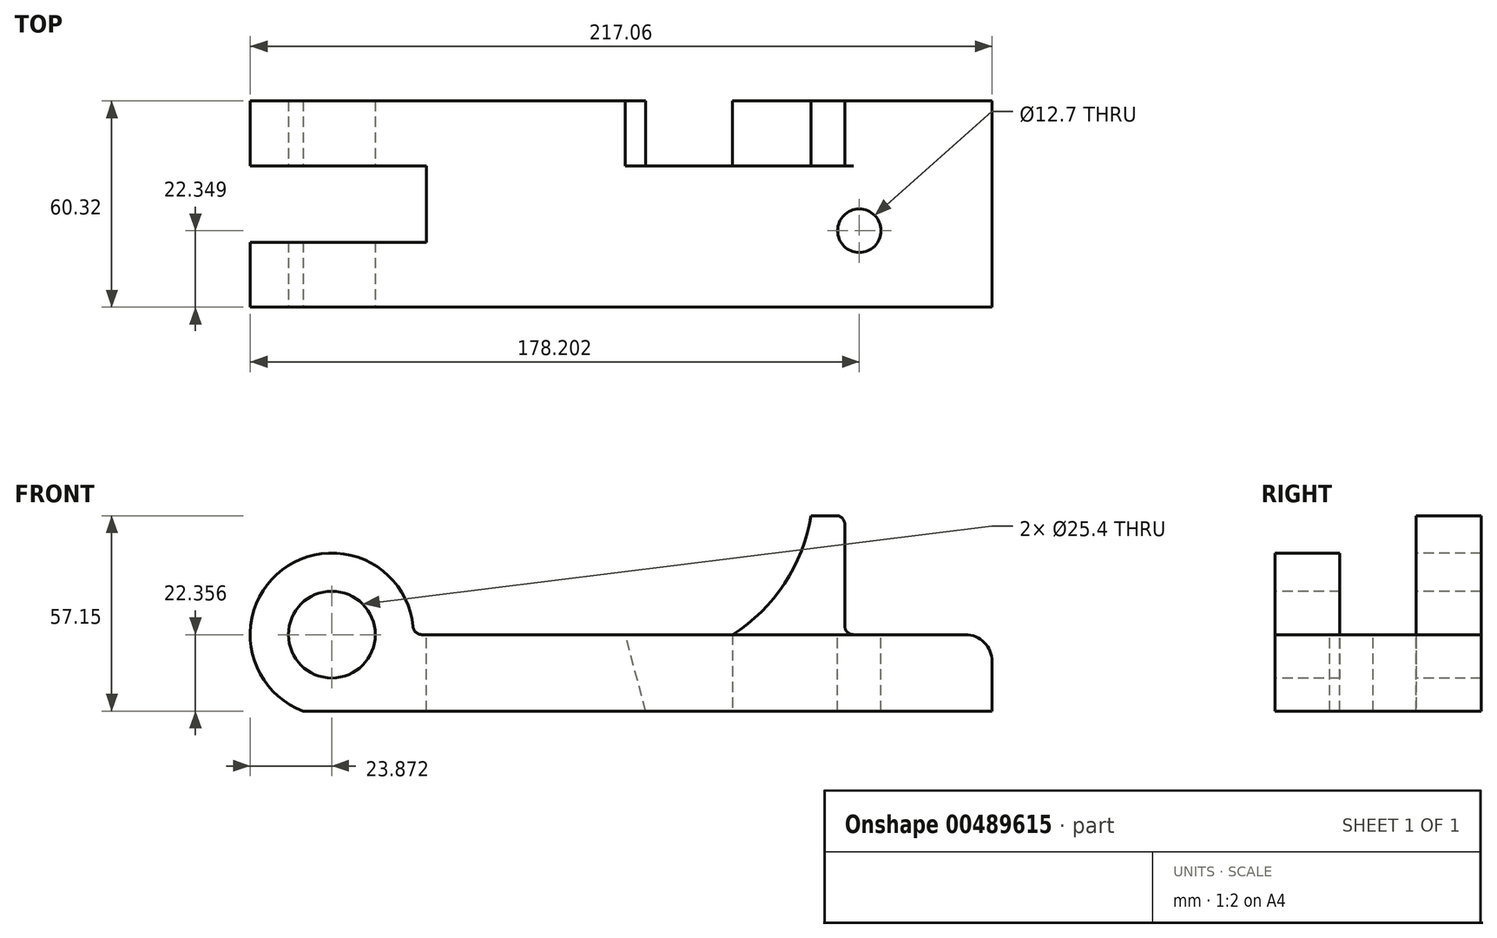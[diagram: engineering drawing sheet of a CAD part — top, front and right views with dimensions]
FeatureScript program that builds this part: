
annotation { "Feature Type Name" : "Feature", "Feature Type Description" : "" }
export const myFeature = defineFeature(function(context is Context, id is Id, definition is map)
    precondition{}
    {
        {
            var Q0;
            Q0=qCreatedBy(makeId("Top.planeOp"),FACE);
            var sketch = newSketch(context, id + "F0", { "sketchPlane" : qUnion([Q0])});
            skLineSegment(sketch, "E0.bottom", {"start": v(-108.28, 30.16) * mm, "end": v(108.28, 30.16) * mm});
            skLineSegment(sketch, "E0.top", {"start": v(-108.28, -30.16) * mm, "end": v(108.28, -30.16) * mm});
            skLineSegment(sketch, "E0.left", {"start": v(-108.28, 30.16) * mm, "end": v(-108.28, -30.16) * mm});
            skLineSegment(sketch, "E0.right", {"start": v(108.28, 30.16) * mm, "end": v(108.28, -30.16) * mm});
            skPoint(sketch, "E0.middle", {"position": v(0, 0) * mm});
            skSolve(sketch);
        }
        {
            var Q0;
            Q0 = qSketchRegion(id + "F0", true);
            extrude(context, id + "F1", {"entities" : qUnion([Q0]), "endBound" : BoundingType.SYMMETRIC, "depth" : 22.35 * mm});
        }
        {
            var Q0;
            Q0=makeQuery(id+"F1.opExtrude","SWEPT_FACE",FACE,{"disambiguationData":[OSD([sQuery(id+"F0.wireOp",EDGE,"E0.top")])]});
            var sketch = newSketch(context, id + "F2", { "sketchPlane" : qUnion([Q0])});
            skLineSegment(sketch, "E1", {"start": v(108.28, -11.18) * mm, "end": v(-85.93, -11.18) * mm, "construction": true});
            skCircle(sketch, "E2", {"center": v(-85.93, 11.18) * mm, "radius": 12.7 * mm});
            skCircle(sketch, "E3", {"center": v(-85.93, 11.18) * mm, "radius": 23.88 * mm});
            skLineSegment(sketch, "E4", {"start": v(-109.8, 11.18) * mm, "end": v(108.28, 11.18) * mm, "construction": true});
            skSolve(sketch);
        }
        {
            var Q0;
            Q0 = qSketchRegion(id + "F2", true);
            var Q1;
            Q1=makeQuery(id+"F1.opExtrude","SWEPT_FACE",FACE,{"disambiguationData":[OSD([sQuery(id+"F0.wireOp",EDGE,"E0.bottom")])]});
            extrude(context, id + "F3", {"entities" : qUnion([Q0]), "operationType" : NewBodyOperationType.ADD, "endBound" : BoundingType.UP_TO_SURFACE, "oppositeDirection" : true, "endBoundEntityFace" : qUnion([Q1]), "depth" : 25.4 * mm});
        }
        {
            var Q0;
            Q0=makeQuery(id+"F3.boolean.opBoolean","MERGE",FACE,{"derivedFrom":[makeQuery(id+"F1.opExtrude","SWEPT_FACE",FACE,{"disambiguationData":[OSD([sQuery(id+"F0.wireOp",EDGE,"E0.top")])]}),makeQuery(id+"F3.opExtrude","CAP_FACE",FACE,{"disambiguationData":[OSD([sQuery(id+"F2.wireOp",EDGE,"E2"),sQuery(id+"F2.wireOp",EDGE,"E3")])],"isStart":true})]});
            var sketch = newSketch(context, id + "F4", { "sketchPlane" : qUnion([Q0])});
            skArc(sketch, "E5.0.0", {"start": v(-94.32, -11.18) * mm, "mid": v(-102.81, -5.7) * mm, "end": v(-108.28, 2.78) * mm});
            skLineSegment(sketch, "E5.0.1", {"start": v(-108.28, 2.78) * mm, "end": v(-108.28, -11.18) * mm});
            skLineSegment(sketch, "E5.0.2", {"start": v(-108.28, -11.18) * mm, "end": v(-94.32, -11.18) * mm});
            skLineSegment(sketch, "E5.1.0", {"start": v(-77.53, -11.18) * mm, "end": v(-94.32, -11.18) * mm});
            skArc(sketch, "E5.1.1", {"start": v(-94.32, -11.18) * mm, "mid": v(-85.93, -12.7) * mm, "end": v(-77.53, -11.18) * mm});
            skLineSegment(sketch, "E6.0.0", {"start": v(-73.23, 11.18) * mm, "end": v(-98.63, 11.18) * mm});
            skArc(sketch, "E6.0.1", {"start": v(-98.63, 11.18) * mm, "mid": v(-85.93, -1.52) * mm, "end": v(-73.23, 11.18) * mm});
            skSolve(sketch);
        }
        {
            var Q0;
            Q0 = qSketchRegion(id + "F4", true);
            extrude(context, id + "F5", {"entities" : qUnion([Q0]), "operationType" : NewBodyOperationType.REMOVE, "endBound" : BoundingType.THROUGH_ALL, "oppositeDirection" : true, "depth" : 25.4 * mm});
        }
        {
            var Q0;
            {var subQ2=sQuery(id+"F0.wireOp",EDGE,"E0.top");var subQ3=sQuery(id+"F0.wireOp",EDGE,"E0.right");var subQ4=sQuery(id+"F0.wireOp",EDGE,"E0.bottom");Q0=makeQuery(id+"F3.boolean.opBoolean","SPLIT",FACE,{"disambiguationData":[TD([makeQuery(id+"F1.opExtrude","SWEPT_FACE",FACE,{"disambiguationData":[OSD([subQ3])]})])],"derivedFrom":makeQuery(id+"F1.opExtrude","CAP_FACE",FACE,{"disambiguationData":[OSD([subQ4,subQ2,sQuery(id+"F0.wireOp",EDGE,"E0.left"),subQ3])],"isStart":false})});}
            var sketch = newSketch(context, id + "F6", { "sketchPlane" : qUnion([Q0])});
            skLineSegment(sketch, "E7.bottom", {"start": v(108.28, -30.16) * mm, "end": v(107.26, -30.16) * mm});
            skLineSegment(sketch, "E7.top", {"start": v(108.28, 30.16) * mm, "end": v(107.26, 30.16) * mm});
            skLineSegment(sketch, "E7.left", {"start": v(108.28, -30.16) * mm, "end": v(108.28, 30.16) * mm});
            skLineSegment(sketch, "E7.right", {"start": v(107.26, -30.16) * mm, "end": v(107.26, 30.16) * mm});
            skLineSegment(sketch, "E8", {"start": v(107.26, 30.16) * mm, "end": v(68.4, 30.16) * mm, "construction": true});
            skLineSegment(sketch, "E9", {"start": v(68.4, 30.16) * mm, "end": v(68.4, 7.81) * mm, "construction": true});
            skLineSegment(sketch, "E10", {"start": v(-62.05, -30.16) * mm, "end": v(-62.05, -11.16) * mm, "construction": true});
            skLineSegment(sketch, "E11", {"start": v(-62.05, 30.16) * mm, "end": v(-62.05, 11.16) * mm, "construction": true});
            skLineSegment(sketch, "E12", {"start": v(-62.05, -11.16) * mm, "end": v(-58.3, -11.16) * mm, "construction": true});
            skLineSegment(sketch, "E13.bottom", {"start": v(-58.3, -11.16) * mm, "end": v(-119.04, -11.16) * mm});
            skLineSegment(sketch, "E13.top", {"start": v(-58.3, 11.16) * mm, "end": v(-119.04, 11.16) * mm});
            skLineSegment(sketch, "E13.left", {"start": v(-58.3, -11.16) * mm, "end": v(-58.3, 11.16) * mm});
            skLineSegment(sketch, "E13.right", {"start": v(-119.04, -11.16) * mm, "end": v(-119.04, 11.16) * mm});
            skLineSegment(sketch, "E14", {"start": v(-62.05, 0) * mm, "end": v(107.26, 0) * mm, "construction": true});
            skCircle(sketch, "E15.MirrorC", {"center": v(68.4, -7.81) * mm, "radius": 6.35 * mm});
            skSolve(sketch);
        }
        {
            var Q0;
            Q0 = qSketchRegion(id + "F6", true);
            extrude(context, id + "F7", {"entities" : qUnion([Q0]), "operationType" : NewBodyOperationType.REMOVE, "endBound" : BoundingType.THROUGH_ALL, "oppositeDirection" : true, "depth" : 25.4 * mm, "hasSecondDirection" : true, "secondDirectionBound" : SecondDirectionBoundingType.THROUGH_ALL, "secondDirectionOppositeDirection" : false, "secondDirectionDepth" : 25.4 * mm});
        }
        {
            var Q0;
            Q0=makeQuery(id+"F3.boolean.opBoolean","MERGE",FACE,{"derivedFrom":[makeQuery(id+"F1.opExtrude","SWEPT_FACE",FACE,{"disambiguationData":[OSD([sQuery(id+"F0.wireOp",EDGE,"E0.bottom")])]}),makeQuery(id+"F3.opExtrude","CAP_FACE",FACE,{"disambiguationData":[OSD([sQuery(id+"F2.wireOp",EDGE,"E2"),sQuery(id+"F2.wireOp",EDGE,"E3")])],"isStart":false})]});
            var sketch = newSketch(context, id + "F8", { "sketchPlane" : qUnion([Q0])});
            skLineSegment(sketch, "E16", {"start": v(85.93, 11.18) * mm, "end": v(-31.32, 11.18) * mm, "construction": true});
            skLineSegment(sketch, "E17", {"start": v(85.93, 11.18) * mm, "end": v(-5.92, 11.18) * mm, "construction": true});
            skLineSegment(sketch, "E18", {"start": v(85.93, 11.18) * mm, "end": v(0.08, 11.18) * mm, "construction": true});
            skLineSegment(sketch, "E19", {"start": v(-31.32, 11.18) * mm, "end": v(-31.32, -11.18) * mm});
            skLineSegment(sketch, "E20", {"start": v(-31.32, -11.18) * mm, "end": v(-5.92, -11.18) * mm});
            skPoint(sketch, "E20.endSnap0", {"position": v(-6.47, -11.18) * mm});
            skLineSegment(sketch, "E21", {"start": v(-5.92, -11.18) * mm, "end": v(0.08, 11.18) * mm});
            skLineSegment(sketch, "E22", {"start": v(0.08, 11.18) * mm, "end": v(-31.32, 11.18) * mm});
            skSolve(sketch);
        }
        {
            var Q0;
            Q0=makeQuery(id+"F3.boolean.opBoolean","MERGE",FACE,{"derivedFrom":[makeQuery(id+"F1.opExtrude","SWEPT_FACE",FACE,{"disambiguationData":[OSD([sQuery(id+"F0.wireOp",EDGE,"E0.bottom")])]}),makeQuery(id+"F3.opExtrude","CAP_FACE",FACE,{"disambiguationData":[OSD([sQuery(id+"F2.wireOp",EDGE,"E2"),sQuery(id+"F2.wireOp",EDGE,"E3")])],"isStart":false})]});
            var sketch = newSketch(context, id + "F9", { "sketchPlane" : qUnion([Q0])});
            skLineSegment(sketch, "E23", {"start": v(85.93, 11.18) * mm, "end": v(-31.32, 11.18) * mm, "construction": true});
            skLineSegment(sketch, "E24", {"start": v(85.93, 11.18) * mm, "end": v(-54.25, 11.18) * mm, "construction": true});
            skLineSegment(sketch, "E25", {"start": v(85.93, 11.18) * mm, "end": v(-64.16, 11.18) * mm, "construction": true});
            skLineSegment(sketch, "E26.bottom", {"start": v(-64.16, -11.18) * mm, "end": v(-54.25, -11.18) * mm});
            skLineSegment(sketch, "E26.top", {"start": v(-64.16, 45.97) * mm, "end": v(-54.25, 45.97) * mm});
            skLineSegment(sketch, "E26.left", {"start": v(-64.16, -11.18) * mm, "end": v(-64.16, 45.97) * mm});
            skLineSegment(sketch, "E26.right", {"start": v(-54.25, -11.18) * mm, "end": v(-54.25, 45.97) * mm});
            skArc(sketch, "E27", {"start": v(-54.25, 45.97) * mm, "mid": v(-46.52, 26.11) * mm, "end": v(-31.32, 11.18) * mm});
            skLineSegment(sketch, "E28", {"start": v(-31.32, 11.18) * mm, "end": v(-54.25, 11.18) * mm});
            skSolve(sketch);
        }
        {
            var Q0;
            Q0 = qSketchRegion(id + "F8", true);
            extrude(context, id + "F10", {"entities" : qUnion([Q0]), "operationType" : NewBodyOperationType.REMOVE, "oppositeDirection" : true, "depth" : 19.05 * mm});
        }
        {
            var Q0;
            Q0 = qSketchRegion(id + "F9", true);
            extrude(context, id + "F11", {"entities" : qUnion([Q0]), "operationType" : NewBodyOperationType.ADD, "oppositeDirection" : true, "depth" : 19.05 * mm});
        }
        {
            var Q0;
            {var subQ0=sQuery(id+"F2.wireOp",EDGE,"E3");var subQ1=makeQuery(id+"F3.opExtrude","SWEPT_FACE",FACE,{"disambiguationData":[OSD([subQ0])]});var subQ2=sQuery(id+"F0.wireOp",EDGE,"E0.bottom");var subQ3=makeQuery(id+"F1.opExtrude","CAP_FACE",FACE,{"disambiguationData":[OSD([subQ2,sQuery(id+"F0.wireOp",EDGE,"E0.top"),sQuery(id+"F0.wireOp",EDGE,"E0.left"),sQuery(id+"F0.wireOp",EDGE,"E0.right")])],"isStart":false});Q0=makeQuery(id+"F7.boolean.opBoolean","SPLIT",EDGE,{"disambiguationData":[TD([makeQuery(id+"F1.opExtrude","SWEPT_FACE",FACE,{"disambiguationData":[OSD([subQ2])]})])],"derivedFrom":makeQuery(id+"F3.boolean.opBoolean","INTERSECT",EDGE,{"derivedFrom":[subQ3,subQ1]})});}
            var Q1;
            {var subQ0=sQuery(id+"F2.wireOp",EDGE,"E3");var subQ1=makeQuery(id+"F3.opExtrude","SWEPT_FACE",FACE,{"disambiguationData":[OSD([subQ0])]});var subQ2=sQuery(id+"F0.wireOp",EDGE,"E0.top");var subQ3=makeQuery(id+"F1.opExtrude","CAP_FACE",FACE,{"disambiguationData":[OSD([sQuery(id+"F0.wireOp",EDGE,"E0.bottom"),subQ2,sQuery(id+"F0.wireOp",EDGE,"E0.left"),sQuery(id+"F0.wireOp",EDGE,"E0.right")])],"isStart":false});Q1=makeQuery(id+"F7.boolean.opBoolean","SPLIT",EDGE,{"disambiguationData":[TD([makeQuery(id+"F1.opExtrude","SWEPT_FACE",FACE,{"disambiguationData":[OSD([subQ2])]})])],"derivedFrom":makeQuery(id+"F3.boolean.opBoolean","INTERSECT",EDGE,{"derivedFrom":[subQ3,subQ1]})});}
            var Q2;
            Q2=makeQuery(id+"F11.opExtrude","SWEPT_EDGE",EDGE,{"disambiguationData":[OSD([sQuery(id+"F9.wireOp",EDGE,"E26.top"),sQuery(id+"F9.wireOp",EDGE,"E26.left")])]});
            var Q3;
            {var subQ2=sQuery(id+"F0.wireOp",EDGE,"E0.top");var subQ3=sQuery(id+"F0.wireOp",EDGE,"E0.right");var subQ4=sQuery(id+"F0.wireOp",EDGE,"E0.bottom");Q3=makeQuery(id+"F11.boolean.opBoolean","INTERSECT",EDGE,{"derivedFrom":[makeQuery(id+"F3.boolean.opBoolean","SPLIT",FACE,{"disambiguationData":[TD([makeQuery(id+"F1.opExtrude","SWEPT_FACE",FACE,{"disambiguationData":[OSD([subQ3])]})])],"derivedFrom":makeQuery(id+"F1.opExtrude","CAP_FACE",FACE,{"disambiguationData":[OSD([subQ4,subQ2,sQuery(id+"F0.wireOp",EDGE,"E0.left"),subQ3])],"isStart":false})}),makeQuery(id+"F11.opExtrude","SWEPT_FACE",FACE,{"disambiguationData":[OSD([sQuery(id+"F9.wireOp",EDGE,"E26.left")])]})]});}
            fillet(context, id + "F12", {"entities" : qUnion([Q0, Q1, Q2, Q3]), "radius" : 2.54 * mm, "tangentPropagation" : true, "allowEdgeOverflow" : false});
        }
        {
            var Q0;
            {var subQ2=sQuery(id+"F0.wireOp",EDGE,"E0.top");var subQ3=sQuery(id+"F0.wireOp",EDGE,"E0.right");var subQ4=sQuery(id+"F0.wireOp",EDGE,"E0.bottom");Q0=makeQuery(id+"F7.boolean.opBoolean","INTERSECT",EDGE,{"derivedFrom":[makeQuery(id+"F3.boolean.opBoolean","SPLIT",FACE,{"disambiguationData":[TD([makeQuery(id+"F1.opExtrude","SWEPT_FACE",FACE,{"disambiguationData":[OSD([subQ3])]})])],"derivedFrom":makeQuery(id+"F1.opExtrude","CAP_FACE",FACE,{"disambiguationData":[OSD([subQ4,subQ2,sQuery(id+"F0.wireOp",EDGE,"E0.left"),subQ3])],"isStart":false})}),makeQuery(id+"F7.opExtrude","SWEPT_FACE",FACE,{"disambiguationData":[OSD([sQuery(id+"F6.wireOp",EDGE,"E7.right")])]})]});}
            fillet(context, id + "F13", {"entities" : qUnion([Q0]), "radius" : 7.87 * mm, "tangentPropagation" : true, "allowEdgeOverflow" : false});
        }
    });
